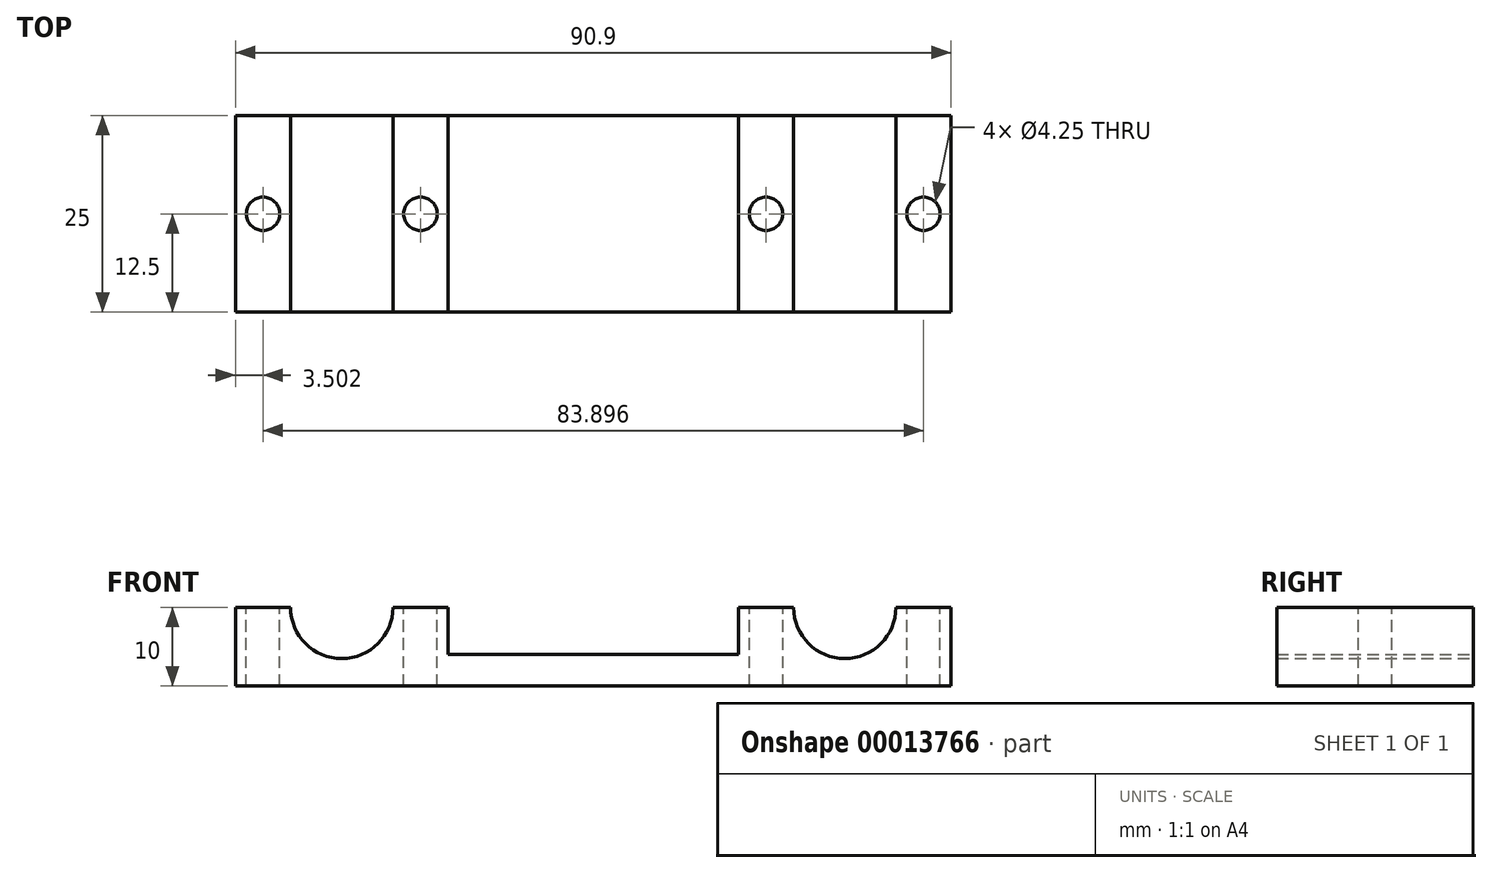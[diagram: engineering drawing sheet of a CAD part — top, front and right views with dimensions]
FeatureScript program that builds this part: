
annotation { "Feature Type Name" : "Feature", "Feature Type Description" : "" }
export const myFeature = defineFeature(function(context is Context, id is Id, definition is map)
    precondition{}
    {
        {
            var Q0;
            Q0=qCreatedBy(makeId("Front.planeOp"),FACE);
            var sketch = newSketch(context, id + "F0", { "sketchPlane" : qUnion([Q0])});
            skLineSegment(sketch, "E0.bottom", {"start": v(0, 0) * mm, "end": v(-45.45, 0) * mm});
            skLineSegment(sketch, "E0.top", {"start": v(-18.45, 10) * mm, "end": v(-18.45, 10) * mm});
            skLineSegment(sketch, "E0.left", {"start": v(0, 0) * mm, "end": v(0, 4) * mm});
            skLineSegment(sketch, "E0.right", {"start": v(-45.45, 0) * mm, "end": v(-45.45, 10) * mm});
            skLineSegment(sketch, "E1.0.MirrorCS", {"start": v(18.45, 10) * mm, "end": v(45.45, 10) * mm});
            skLineSegment(sketch, "E2.0.MirrorCS", {"start": v(45.45, 0) * mm, "end": v(45.45, 10) * mm});
            skLineSegment(sketch, "E3.0.MirrorCS", {"start": v(0, 0) * mm, "end": v(45.45, 0) * mm});
            skCircle(sketch, "E4", {"center": v(-31.95, 10) * mm, "radius": 6.5 * mm});
            skCircle(sketch, "E5.0.MirrorC", {"center": v(31.95, 10) * mm, "radius": 6.5 * mm});
            skLineSegment(sketch, "E6", {"start": v(-18.45, 10) * mm, "end": v(-18.45, 4) * mm});
            skLineSegment(sketch, "E7.0.MirrorCS", {"start": v(18.45, 4) * mm, "end": v(0, 4) * mm});
            skLineSegment(sketch, "E8.0.MirrorCS", {"start": v(18.45, 10) * mm, "end": v(18.45, 4) * mm});
            skLineSegment(sketch, "E9", {"start": v(-18.45, 4) * mm, "end": v(0, 4) * mm});
            skLineSegment(sketch, "E10", {"start": v(-25.45, 10) * mm, "end": v(-38.45, 10) * mm});
            skLineSegment(sketch, "E11", {"start": v(-18.45, 10) * mm, "end": v(-25.45, 10) * mm});
            skLineSegment(sketch, "E12", {"start": v(-45.45, 10) * mm, "end": v(-45.45, 10) * mm});
            skLineSegment(sketch, "E13", {"start": v(-38.45, 10) * mm, "end": v(-45.45, 10) * mm});
            skSolve(sketch);
        }
        {
            var Q0;
            Q0=makeQuery(id+"F0.imprint","IMPRINT",FACE,{"disambiguationData":[TD([[makeQuery(id+"F0.imprint","IMPRINT",EDGE,{"derivedFrom":sQuery(id+"F0.wireOp",EDGE,"E0.bottom")}),-1.0]])]});
            var Q1;
            Q1=makeQuery(id+"F0.imprint","IMPRINT",FACE,{"disambiguationData":[TD([[makeQuery(id+"F0.imprint","IMPRINT",EDGE,{"derivedFrom":sQuery(id+"F0.wireOp",EDGE,"E0.left")}),-1.0]])]});
            extrude(context, id + "F1", {"entities" : qUnion([Q0, Q1]), "depth" : 25 * mm});
        }
        {
            var Q0;
            Q0=makeQuery(id+"F1.opExtrude","SWEPT_FACE",FACE,{"disambiguationData":[OSD([sQuery(id+"F0.wireOp",EDGE,"E13")])]});
            var sketch = newSketch(context, id + "F2", { "sketchPlane" : qUnion([Q0])});
            skLineSegment(sketch, "E14", {"start": v(-41.95, 0) * mm, "end": v(-41.95, -25) * mm, "construction": true});
            skCircle(sketch, "E15", {"center": v(-41.95, -12.5) * mm, "radius": 2.12 * mm});
            skCircle(sketch, "E16.0.MirrorC", {"center": v(41.95, -12.5) * mm, "radius": 2.12 * mm});
            skSolve(sketch);
        }
        {
            var Q0;
            Q0 = qSketchRegion(id + "F2", true);
            extrude(context, id + "F3", {"entities" : qUnion([Q0]), "operationType" : NewBodyOperationType.REMOVE, "endBound" : BoundingType.THROUGH_ALL, "oppositeDirection" : true, "depth" : 25 * mm});
        }
        {
            var Q0;
            Q0=makeQuery(id+"F1.opExtrude","SWEPT_FACE",FACE,{"disambiguationData":[OSD([sQuery(id+"F0.wireOp",EDGE,"E11")])]});
            var sketch = newSketch(context, id + "F4", { "sketchPlane" : qUnion([Q0])});
            skLineSegment(sketch, "E17", {"start": v(-21.95, 0) * mm, "end": v(-21.95, -25) * mm, "construction": true});
            skCircle(sketch, "E18", {"center": v(-21.95, -12.5) * mm, "radius": 2.12 * mm});
            skCircle(sketch, "E19.0.MirrorC", {"center": v(21.95, -12.5) * mm, "radius": 2.12 * mm});
            skSolve(sketch);
        }
        {
            var Q0;
            Q0 = qSketchRegion(id + "F4", true);
            extrude(context, id + "F5", {"entities" : qUnion([Q0]), "operationType" : NewBodyOperationType.REMOVE, "endBound" : BoundingType.THROUGH_ALL, "oppositeDirection" : true, "depth" : 25 * mm});
        }
    });
